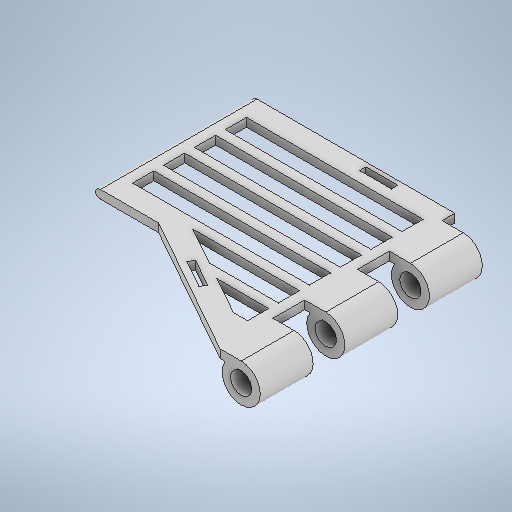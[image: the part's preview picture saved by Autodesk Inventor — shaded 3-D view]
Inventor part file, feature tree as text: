
AUTODESK INVENTOR PART (.ipt)
format: ipt  version: 2025.1 (Build 291241020, 241B)  size: 411,648 bytes
history: native  units: mm
features: extrude x7, sketch x7, fillet x2, sweep x1, pattern_linear x1, projected_geometry x1
ambient origin geometry x8: Origin, YZ Plane, XZ Plane, XY Plane, X Axis, Y Axis, Z Axis, Center Point
bodies: Solid1 (feature_tree)
feature tree (19):
  extrude  "Extrusion1"  Depth=10.0mm
  sweep  "Sweep1"
  fillet  "Fillet1"  Radius=105.0mm
  extrude  "Extrusion7"  Depth=68.0mm
  fillet  "Fillet2"  Radius=96.0mm
  extrude  "Extrusion9"  Depth=2.5mm
  extrude  "Extrusion11"  Depth=5.0mm
  extrude  "Extrusion12"  Depth=15.0mm
  extrude  "Extrusion16"  Depth=25.0mm
  pattern_linear  "Rectangular Pattern2"  Spacing1=25.0mm  [1 undecoded]
  extrude  "Extrusion14"  Depth=15.0mm
  projected_geometry  "Projected Loop1"
  sketch  "Sketch3"  dims[d2=4.0mm d3=0.0mm d5=10.0mm]
  sketch  "Sketch11"  dims[d7=0.0mm d8=0.0mm d54=2.5mm d56=105.0mm]
  sketch  "Sketch13"  dims[d57=68.0mm d58=30.0mm d61=96.0mm]
  sketch  "Sketch15"  dims[d64=10.0mm d65=0.0mm d66=2.5mm]
  sketch  "Sketch17"  dims[d67=6.0mm d75=5.0mm]
  sketch  "Sketch19"  dims[d76=10.0mm d78=15.0mm]
  sketch  "Sketch21"  dims[d79=20.0mm d80=25.0mm d81=25.0mm d82=15.0mm d83=50.0mm d84=0.0mm d92=3.0mm d93=15.0mm d95=3.0mm d96=3.0mm d98=29.0mm d99=0.0mm d100=0.0mm d104=15.0mm d105=3.0mm d106=2.0mm d107=25.0mm d108=0.0mm d109=0.0mm d120=10.0mm d123=10.0mm d125=10.0mm d126=4.6mm d127=10.0mm d128=0.0mm d129=0.0mm d132=10.0mm d133=10.0mm d134=5.0mm d135=5.0mm d136=0.0mm d137=0.0mm d138=40.0mm d140=14.6mm d141=4.6mm d142=10.0mm d42=0.5mm d43=0.872665mm d44=0.5mm d45=0.872665mm]
note: 1 required parameter value undecoded (feature->parameter linkage not recoverable at this tier; creation-order binding heuristic only, values carry confidence <= 0.55)
